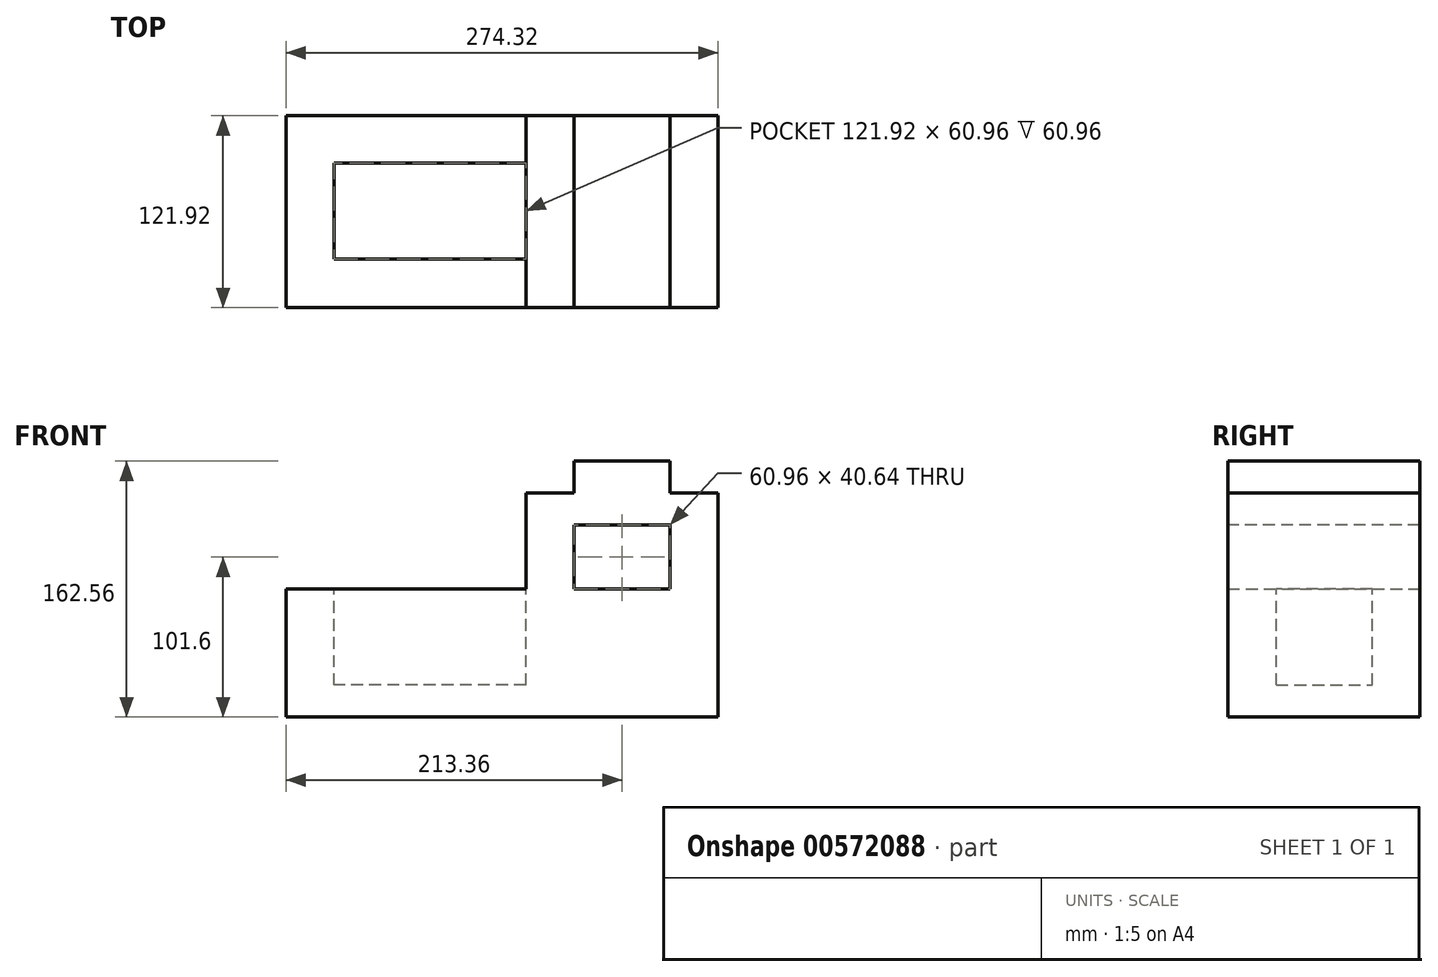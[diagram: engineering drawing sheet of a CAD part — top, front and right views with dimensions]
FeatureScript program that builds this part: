
annotation { "Feature Type Name" : "Feature", "Feature Type Description" : "" }
export const myFeature = defineFeature(function(context is Context, id is Id, definition is map)
    precondition{}
    {
        {
            var Q0;
            Q0=qCreatedBy(makeId("Front.planeOp"),FACE);
            var sketch = newSketch(context, id + "F0", { "sketchPlane" : qUnion([Q0])});
            skLineSegment(sketch, "E0.bottom", {"start": v(137.16, 40.64) * mm, "end": v(-137.16, 40.64) * mm});
            skLineSegment(sketch, "E0.top", {"start": v(137.16, -40.64) * mm, "end": v(-137.16, -40.64) * mm});
            skLineSegment(sketch, "E0.left", {"start": v(137.16, 40.64) * mm, "end": v(137.16, -40.64) * mm});
            skLineSegment(sketch, "E0.right", {"start": v(-137.16, 40.64) * mm, "end": v(-137.16, -40.64) * mm});
            skPoint(sketch, "E0.middle", {"position": v(0, 0) * mm});
            skLineSegment(sketch, "E1", {"start": v(137.16, 40.64) * mm, "end": v(137.16, 101.6) * mm});
            skLineSegment(sketch, "E2", {"start": v(137.16, 101.6) * mm, "end": v(106.68, 101.6) * mm});
            skLineSegment(sketch, "E3", {"start": v(106.68, 101.6) * mm, "end": v(106.68, 121.92) * mm});
            skLineSegment(sketch, "E4", {"start": v(106.68, 121.92) * mm, "end": v(45.72, 121.92) * mm});
            skLineSegment(sketch, "E5", {"start": v(45.72, 121.92) * mm, "end": v(45.72, 101.6) * mm});
            skLineSegment(sketch, "E6", {"start": v(45.72, 101.6) * mm, "end": v(15.24, 101.6) * mm});
            skLineSegment(sketch, "E7", {"start": v(15.24, 101.6) * mm, "end": v(15.24, 40.64) * mm});
            skSolve(sketch);
        }
        {
            var Q0;
            Q0=makeQuery(id+"F0.imprint","IMPRINT",FACE,{"disambiguationData":[TD([[makeQuery(id+"F0.imprint","IMPRINT",EDGE,{"derivedFrom":sQuery(id+"F0.wireOp",EDGE,"E0.top")}),-1.0]])]});
            var Q1;
            {var subQ0=sQuery(id+"F0.wireOp",EDGE,"E1");Q1=makeQuery(id+"F0.imprint","IMPRINT",FACE,{"disambiguationData":[TD([[makeQuery(id+"F0.imprint","IMPRINT",EDGE,{"derivedFrom":subQ0}),1.0]])]});}
            extrude(context, id + "F1", {"entities" : qUnion([Q0, Q1]), "depth" : 121.92 * mm, "offsetDistance" : 25.4 * mm});
        }
        {
            var Q0;
            Q0=makeQuery(id+"F1.opExtrude","SWEPT_FACE",FACE,{"disambiguationData":[OSD([sQuery(id+"F0.wireOp",EDGE,"E0.bottom")])]});
            var sketch = newSketch(context, id + "F2", { "sketchPlane" : qUnion([Q0])});
            skLineSegment(sketch, "E8", {"start": v(15.24, -30.15) * mm, "end": v(15.24, -91.11) * mm});
            skLineSegment(sketch, "E9", {"start": v(15.24, -30.15) * mm, "end": v(-45.72, -30.15) * mm});
            skLineSegment(sketch, "E10", {"start": v(-45.72, -30.15) * mm, "end": v(-106.68, -30.15) * mm});
            skLineSegment(sketch, "E11", {"start": v(-106.68, -30.15) * mm, "end": v(-106.68, -91.11) * mm});
            skLineSegment(sketch, "E12", {"start": v(-106.68, -91.11) * mm, "end": v(15.24, -91.11) * mm});
            skSolve(sketch);
        }
        {
            var Q0;
            Q0=makeQuery(id+"F2.imprint","IMPRINT",FACE,{"disambiguationData":[TD([[makeQuery(id+"F2.imprint","IMPRINT",EDGE,{"derivedFrom":sQuery(id+"F2.wireOp",EDGE,"E8")}),1.0]])]});
            extrude(context, id + "F3", {"entities" : qUnion([Q0]), "operationType" : NewBodyOperationType.REMOVE, "oppositeDirection" : true, "depth" : 60.96 * mm, "offsetDistance" : 25.4 * mm});
        }
        {
            var Q0;
            Q0=makeQuery(id+"F1.opExtrude","CAP_FACE",FACE,{"disambiguationData":[OSD([sQuery(id+"F0.wireOp",EDGE,"E0.bottom"),sQuery(id+"F0.wireOp",EDGE,"E0.top"),sQuery(id+"F0.wireOp",EDGE,"E0.left"),sQuery(id+"F0.wireOp",EDGE,"E0.right"),sQuery(id+"F0.wireOp",EDGE,"E1"),sQuery(id+"F0.wireOp",EDGE,"E2"),sQuery(id+"F0.wireOp",EDGE,"E3"),sQuery(id+"F0.wireOp",EDGE,"E4"),sQuery(id+"F0.wireOp",EDGE,"E5"),sQuery(id+"F0.wireOp",EDGE,"E6"),sQuery(id+"F0.wireOp",EDGE,"E7")])],"isStart":false});
            var sketch = newSketch(context, id + "F4", { "sketchPlane" : qUnion([Q0])});
            skLineSegment(sketch, "E13", {"start": v(106.68, 81.28) * mm, "end": v(45.72, 81.28) * mm});
            skLineSegment(sketch, "E14", {"start": v(45.72, 81.28) * mm, "end": v(45.72, 40.64) * mm});
            skLineSegment(sketch, "E15", {"start": v(45.72, 40.64) * mm, "end": v(106.68, 40.64) * mm});
            skLineSegment(sketch, "E16", {"start": v(106.68, 40.64) * mm, "end": v(106.68, 81.28) * mm});
            skSolve(sketch);
        }
        {
            var Q0;
            Q0=makeQuery(id+"F4.imprint","IMPRINT",FACE,{"disambiguationData":[TD([[makeQuery(id+"F4.imprint","IMPRINT",EDGE,{"derivedFrom":sQuery(id+"F4.wireOp",EDGE,"E13")}),1.0]])]});
            extrude(context, id + "F5", {"entities" : qUnion([Q0]), "operationType" : NewBodyOperationType.REMOVE, "endBound" : BoundingType.THROUGH_ALL, "oppositeDirection" : true, "depth" : 25.4 * mm, "offsetDistance" : 25.4 * mm});
        }
    });
